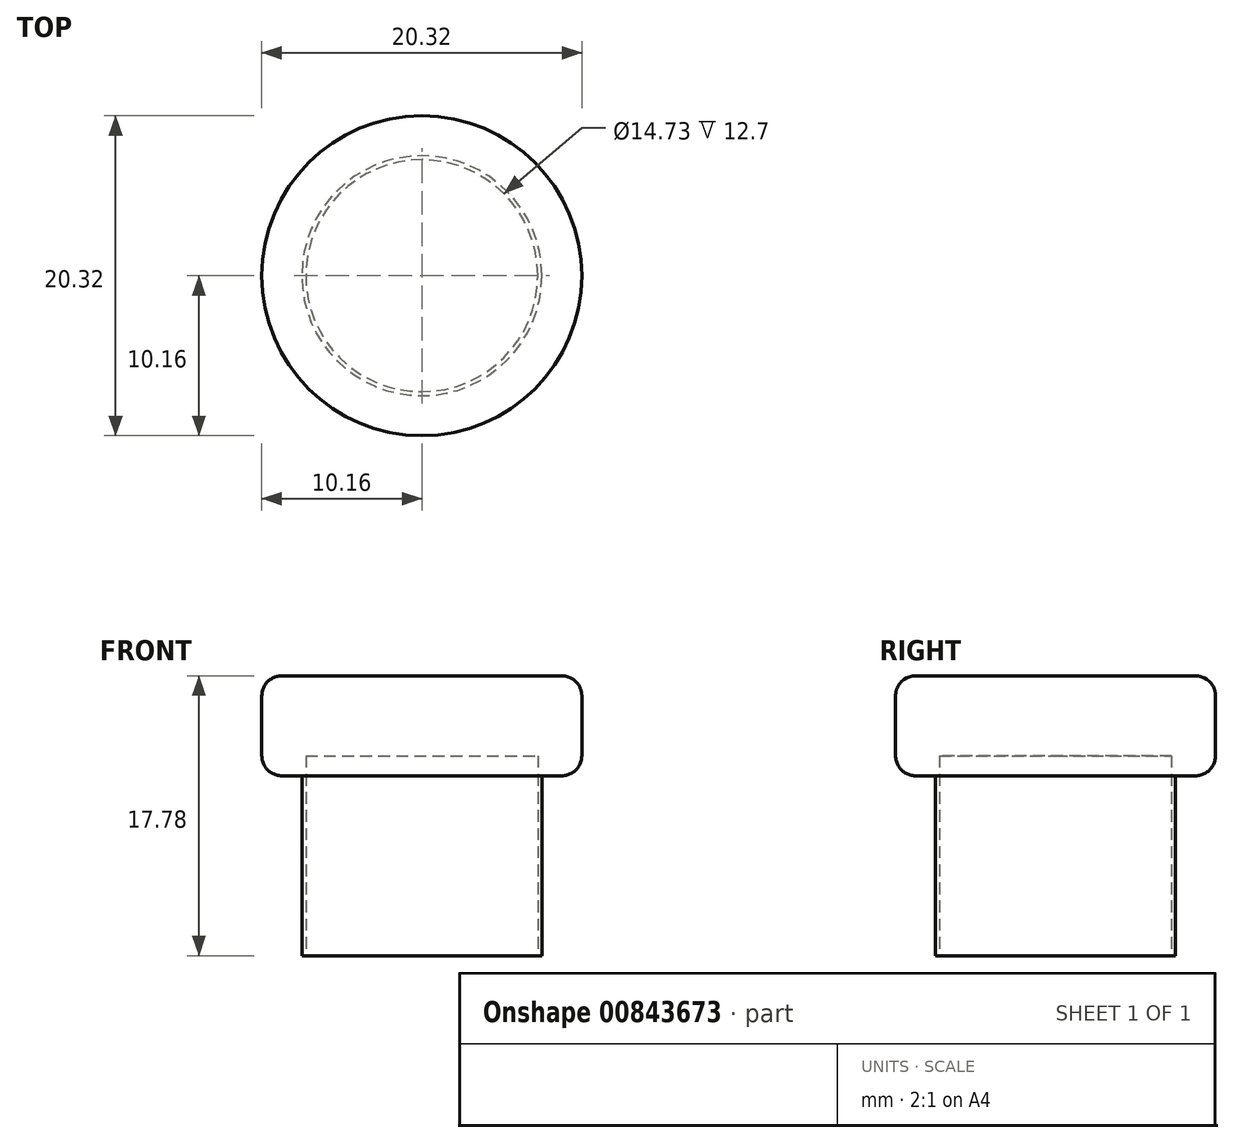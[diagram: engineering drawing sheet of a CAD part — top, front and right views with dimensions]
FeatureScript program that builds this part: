
annotation { "Feature Type Name" : "Feature", "Feature Type Description" : "" }
export const myFeature = defineFeature(function(context is Context, id is Id, definition is map)
    precondition{}
    {
        {
            var Q0;
            Q0=qCreatedBy(makeId("Right.planeOp"),FACE);
            var sketch = newSketch(context, id + "F0", { "sketchPlane" : qUnion([Q0])});
            skLineSegment(sketch, "E0.bottom", {"start": v(0, 0) * mm, "end": v(7.62, 0) * mm});
            skLineSegment(sketch, "E0.top", {"start": v(0, 11.43) * mm, "end": v(7.62, 11.43) * mm});
            skLineSegment(sketch, "E0.left", {"start": v(0, 0) * mm, "end": v(0, 11.43) * mm});
            skLineSegment(sketch, "E0.right", {"start": v(7.62, 0) * mm, "end": v(7.62, 11.43) * mm});
            skLineSegment(sketch, "E1.bottom", {"start": v(0, 11.43) * mm, "end": v(10.16, 11.43) * mm});
            skLineSegment(sketch, "E1.top", {"start": v(0, 17.78) * mm, "end": v(10.16, 17.78) * mm});
            skLineSegment(sketch, "E1.left", {"start": v(0, 11.43) * mm, "end": v(0, 17.78) * mm});
            skLineSegment(sketch, "E1.right", {"start": v(10.16, 11.43) * mm, "end": v(10.16, 17.78) * mm});
            skSolve(sketch);
        }
        {
            var Q0;
            {var subQ0=makeQuery(id+"F0.imprint","IMPRINT",EDGE,{"derivedFrom":sQuery(id+"F0.wireOp",EDGE,"E0.top")});Q0=qUnion([makeQuery(id+"F0.imprint","IMPRINT",FACE,{"disambiguationData":[TD([[makeQuery(id+"F0.imprint","IMPRINT",EDGE,{"derivedFrom":sQuery(id+"F0.wireOp",EDGE,"E0.bottom")}),1.0]])]}),makeQuery(id+"F0.imprint","IMPRINT",FACE,{"disambiguationData":[TD([[subQ0,1.0]])]})]);}
            var Q1;
            Q1=sQuery(id+"F0.wireOp",EDGE,"E0.left");
            revolve(context, id + "F1", {"surfaceOperationType" : NewSurfaceOperationType.NEW, "entities" : qUnion([Q0]), "axis" : qUnion([Q1]), "revolveType" : RevolveType.FULL});
        }
        {
            var Q0;
            Q0=makeQuery(id+"F1.opRevolve","SWEPT_FACE",FACE,{"disambiguationData":[OSD([sQuery(id+"F0.wireOp",EDGE,"E1.right")])]});
            fillet(context, id + "F2", {"entities" : qUnion([Q0]), "radius" : 1.27 * mm, "tangentPropagation" : true, "allowEdgeOverflow" : false});
        }
        {
            var Q0;
            Q0=makeQuery(id+"F1.opRevolve","SWEPT_FACE",FACE,{"disambiguationData":[OSD([sQuery(id+"F0.wireOp",EDGE,"E0.bottom")])]});
            var sketch = newSketch(context, id + "F3", { "sketchPlane" : qUnion([Q0])});
            skCircle(sketch, "E2", {"center": v(0, 0) * mm, "radius": 7.37 * mm});
            skSolve(sketch);
        }
        {
            var Q0;
            Q0=makeQuery(id+"F3.imprint","IMPRINT",FACE,{"disambiguationData":[TD([[makeQuery(id+"F3.imprint","IMPRINT",EDGE,{"derivedFrom":sQuery(id+"F3.wireOp",EDGE,"E2")}),1.0]])]});
            extrude(context, id + "F4", {"entities" : qUnion([Q0]), "operationType" : NewBodyOperationType.REMOVE, "oppositeDirection" : true, "depth" : 25.4 * mm / 2, "offsetDistance" : 25.4 * mm});
        }
    });
